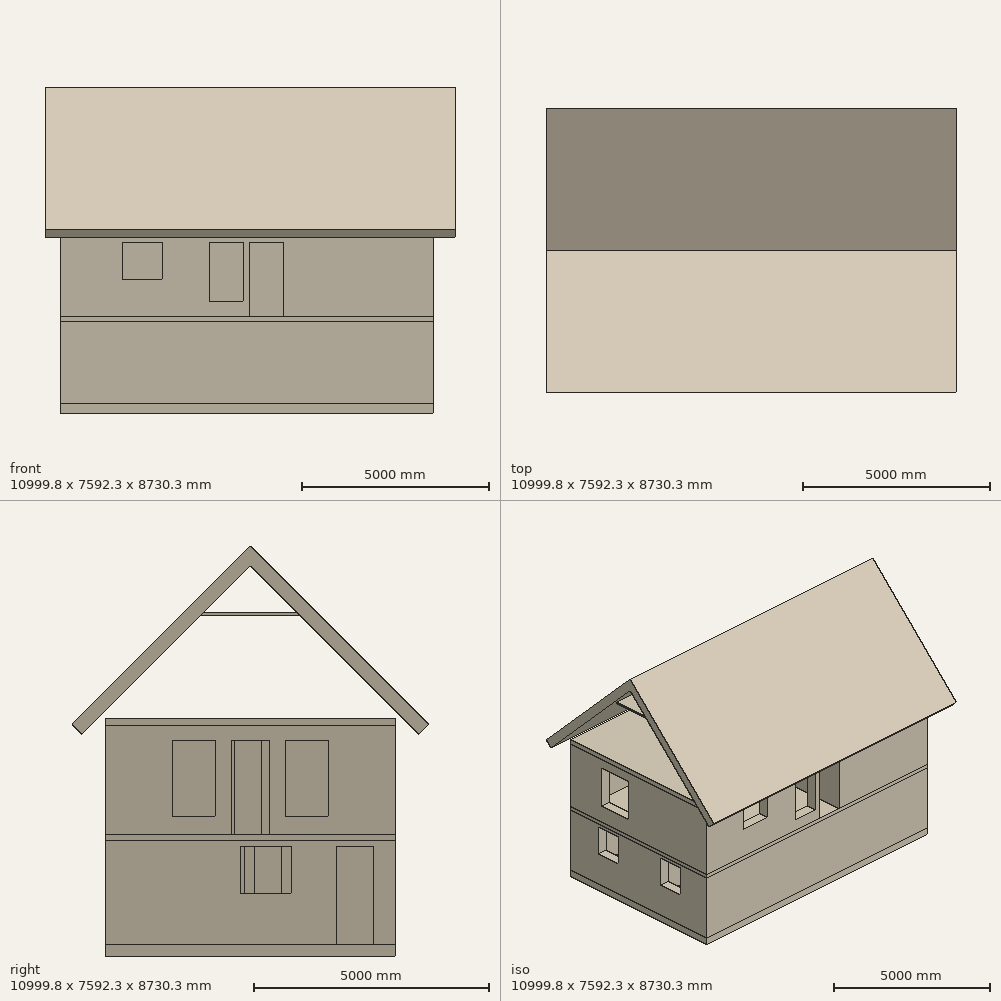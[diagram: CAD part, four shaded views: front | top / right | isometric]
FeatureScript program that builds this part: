
annotation { "Feature Type Name" : "Feature", "Feature Type Description" : "" }
export const myFeature = defineFeature(function(context is Context, id is Id, definition is map)
    precondition{}
    {
        {
            var Q0;
            Q0=qCreatedBy(makeId("Top.planeOp"),FACE);
            var sketch = newSketch(context, id + "F0", { "sketchPlane" : qUnion([Q0])});
            skLineSegment(sketch, "E0", {"start": v(0, 0) * mm, "end": v(-9312, 0) * mm});
            skLineSegment(sketch, "E1", {"start": v(0, 0) * mm, "end": v(0, -5472) * mm});
            skLineSegment(sketch, "E2", {"start": v(0, -5472) * mm, "end": v(-9312, -5472) * mm});
            skLineSegment(sketch, "E3", {"start": v(-9312, -5472) * mm, "end": v(-9312, 0) * mm});
            skLineSegment(sketch, "E4.0", {"start": v(348, 348) * mm, "end": v(-9660, 348) * mm});
            skLineSegment(sketch, "E4.1", {"start": v(348, 348) * mm, "end": v(348, -5820) * mm});
            skLineSegment(sketch, "E4.2", {"start": v(348, -5820) * mm, "end": v(-9660, -5820) * mm});
            skLineSegment(sketch, "E4.3", {"start": v(-9660, -5820) * mm, "end": v(-9660, 348) * mm});
            skSolve(sketch);
        }
        {
            var Q0;
            Q0=makeQuery(id+"F0.imprint","IMPRINT",FACE,{"disambiguationData":[TD([[makeQuery(id+"F0.imprint","IMPRINT",EDGE,{"derivedFrom":sQuery(id+"F0.wireOp",EDGE,"E0")}),-1.0]])]});
            extrude(context, id + "F1", {"entities" : qUnion([Q0]), "depth" : 2320 * mm});
        }
        {
            var Q0;
            Q0=qCreatedBy(makeId("Top.planeOp"),FACE);
            var sketch = newSketch(context, id + "F2", { "sketchPlane" : qUnion([Q0])});
            skLineSegment(sketch, "E5.bottom", {"start": v(-3552, 0) * mm, "end": v(-3660, 0) * mm});
            skLineSegment(sketch, "E5.top", {"start": v(-3552, -5472) * mm, "end": v(-3660, -5472) * mm});
            skLineSegment(sketch, "E5.left", {"start": v(-3552, 0) * mm, "end": v(-3552, -5472) * mm});
            skLineSegment(sketch, "E5.right", {"start": v(-3660, 0) * mm, "end": v(-3660, -5472) * mm});
            skLineSegment(sketch, "E6.bottom", {"start": v(-5652, 0) * mm, "end": v(-5760, 0) * mm});
            skLineSegment(sketch, "E6.top", {"start": v(-5652, -5472) * mm, "end": v(-5760, -5472) * mm});
            skLineSegment(sketch, "E6.left", {"start": v(-5652, 0) * mm, "end": v(-5652, -5472) * mm});
            skLineSegment(sketch, "E6.right", {"start": v(-5760, 0) * mm, "end": v(-5760, -5472) * mm});
            skSolve(sketch);
        }
        {
            var Q0;
            Q0 = qSketchRegion(id + "F2", true);
            var Q1;
            Q1=makeQuery(id+"F1.opExtrude","CAP_FACE",FACE,{"disambiguationData":[OSD([sQuery(id+"F0.wireOp",EDGE,"E0"),sQuery(id+"F0.wireOp",EDGE,"E1"),sQuery(id+"F0.wireOp",EDGE,"E2"),sQuery(id+"F0.wireOp",EDGE,"E3"),sQuery(id+"F0.wireOp",EDGE,"E4.0"),sQuery(id+"F0.wireOp",EDGE,"E4.1"),sQuery(id+"F0.wireOp",EDGE,"E4.2"),sQuery(id+"F0.wireOp",EDGE,"E4.3")])],"isStart":false});
            extrude(context, id + "F3", {"entities" : qUnion([Q0]), "operationType" : NewBodyOperationType.ADD, "endBound" : BoundingType.UP_TO_SURFACE, "endBoundEntityFace" : qUnion([Q1]), "depth" : 25 * mm});
        }
        {
            var Q0;
            Q0=qCreatedBy(makeId("Top.planeOp"),FACE);
            var sketch = newSketch(context, id + "F4", { "sketchPlane" : qUnion([Q0])});
            skLineSegment(sketch, "E7.bottom", {"start": v(-9312, -3072) * mm, "end": v(-5760, -3072) * mm});
            skLineSegment(sketch, "E7.top", {"start": v(-9312, -3180) * mm, "end": v(-5760, -3180) * mm});
            skLineSegment(sketch, "E7.left", {"start": v(-9312, -3072) * mm, "end": v(-9312, -3180) * mm});
            skLineSegment(sketch, "E7.right", {"start": v(-5760, -3072) * mm, "end": v(-5760, -3180) * mm});
            skSolve(sketch);
        }
        {
            var Q0;
            Q0 = qSketchRegion(id + "F4", true);
            var Q1;
            Q1=makeQuery(id+"F3.boolean.opBoolean","MERGE",FACE,{"derivedFrom":[makeQuery(id+"F1.opExtrude","CAP_FACE",FACE,{"disambiguationData":[OSD([sQuery(id+"F0.wireOp",EDGE,"E0"),sQuery(id+"F0.wireOp",EDGE,"E1"),sQuery(id+"F0.wireOp",EDGE,"E2"),sQuery(id+"F0.wireOp",EDGE,"E3"),sQuery(id+"F0.wireOp",EDGE,"E4.0"),sQuery(id+"F0.wireOp",EDGE,"E4.1"),sQuery(id+"F0.wireOp",EDGE,"E4.2"),sQuery(id+"F0.wireOp",EDGE,"E4.3")])],"isStart":false}),makeQuery(id+"F3.opExtrude","CAP_FACE",FACE,{"disambiguationData":[OSD([sQuery(id+"F2.wireOp",EDGE,"E5.bottom"),sQuery(id+"F2.wireOp",EDGE,"E5.top"),sQuery(id+"F2.wireOp",EDGE,"E5.left"),sQuery(id+"F2.wireOp",EDGE,"E5.right")])],"isStart":false}),makeQuery(id+"F3.opExtrude","CAP_FACE",FACE,{"disambiguationData":[OSD([sQuery(id+"F2.wireOp",EDGE,"E6.bottom"),sQuery(id+"F2.wireOp",EDGE,"E6.top"),sQuery(id+"F2.wireOp",EDGE,"E6.left"),sQuery(id+"F2.wireOp",EDGE,"E6.right")])],"isStart":false})]});
            extrude(context, id + "F5", {"entities" : qUnion([Q0]), "operationType" : NewBodyOperationType.ADD, "endBound" : BoundingType.UP_TO_SURFACE, "endBoundEntityFace" : qUnion([Q1]), "depth" : 25 * mm});
        }
        {
            var Q0;
            Q0=makeQuery(id+"F1.opExtrude","SWEPT_FACE",FACE,{"disambiguationData":[OSD([sQuery(id+"F0.wireOp",EDGE,"E4.2")])]});
            var sketch = newSketch(context, id + "F6", { "sketchPlane" : qUnion([Q0])});
            skLineSegment(sketch, "E8.bottom", {"start": v(-4572, 0) * mm, "end": v(-3660, 0) * mm});
            skLineSegment(sketch, "E8.top", {"start": v(-4572, 2000) * mm, "end": v(-3660, 2000) * mm});
            skLineSegment(sketch, "E8.left", {"start": v(-4572, 0) * mm, "end": v(-4572, 2000) * mm});
            skLineSegment(sketch, "E8.right", {"start": v(-3660, 0) * mm, "end": v(-3660, 2000) * mm});
            skLineSegment(sketch, "E9.bottom", {"start": v(-4740, 2000) * mm, "end": v(-5652, 2000) * mm});
            skLineSegment(sketch, "E9.top", {"start": v(-4740, 400) * mm, "end": v(-5652, 400) * mm});
            skLineSegment(sketch, "E9.left", {"start": v(-4740, 2000) * mm, "end": v(-4740, 400) * mm});
            skLineSegment(sketch, "E9.right", {"start": v(-5652, 2000) * mm, "end": v(-5652, 400) * mm});
            skLineSegment(sketch, "E10.bottom", {"start": v(-6912, 2000) * mm, "end": v(-7992, 2000) * mm});
            skLineSegment(sketch, "E10.top", {"start": v(-6912, 1000) * mm, "end": v(-7992, 1000) * mm});
            skLineSegment(sketch, "E10.left", {"start": v(-6912, 2000) * mm, "end": v(-6912, 1000) * mm});
            skLineSegment(sketch, "E10.right", {"start": v(-7992, 2000) * mm, "end": v(-7992, 1000) * mm});
            skSolve(sketch);
        }
        {
            var Q0;
            Q0 = qSketchRegion(id + "F6", true);
            extrude(context, id + "F7", {"entities" : qUnion([Q0]), "operationType" : NewBodyOperationType.REMOVE, "endBound" : BoundingType.UP_TO_NEXT, "oppositeDirection" : true, "depth" : 25 * mm});
        }
        {
            var Q0;
            Q0=makeQuery(id+"F1.opExtrude","SWEPT_FACE",FACE,{"disambiguationData":[OSD([sQuery(id+"F0.wireOp",EDGE,"E1")])]});
            var sketch = newSketch(context, id + "F8", { "sketchPlane" : qUnion([Q0])});
            skLineSegment(sketch, "E11.bottom", {"start": v(2340, 0) * mm, "end": v(3132, 0) * mm});
            skLineSegment(sketch, "E11.top", {"start": v(2340, 2000) * mm, "end": v(3132, 2000) * mm});
            skLineSegment(sketch, "E11.left", {"start": v(2340, 0) * mm, "end": v(2340, 2000) * mm});
            skLineSegment(sketch, "E11.right", {"start": v(3132, 0) * mm, "end": v(3132, 2000) * mm});
            skLineSegment(sketch, "E12.bottom", {"start": v(4392, 2000) * mm, "end": v(3480, 2000) * mm});
            skLineSegment(sketch, "E12.top", {"start": v(4392, 400) * mm, "end": v(3480, 400) * mm});
            skLineSegment(sketch, "E12.left", {"start": v(4392, 2000) * mm, "end": v(4392, 400) * mm});
            skLineSegment(sketch, "E12.right", {"start": v(3480, 2000) * mm, "end": v(3480, 400) * mm});
            skLineSegment(sketch, "E13.bottom", {"start": v(1992, 2000) * mm, "end": v(1080, 2000) * mm});
            skLineSegment(sketch, "E13.top", {"start": v(1992, 400) * mm, "end": v(1080, 400) * mm});
            skLineSegment(sketch, "E13.left", {"start": v(1992, 2000) * mm, "end": v(1992, 400) * mm});
            skLineSegment(sketch, "E13.right", {"start": v(1080, 2000) * mm, "end": v(1080, 400) * mm});
            skSolve(sketch);
        }
        {
            var Q0;
            Q0 = qSketchRegion(id + "F8", true);
            extrude(context, id + "F9", {"entities" : qUnion([Q0]), "operationType" : NewBodyOperationType.REMOVE, "endBound" : BoundingType.UP_TO_NEXT, "oppositeDirection" : true, "depth" : 25 * mm});
        }
        {
            var Q0;
            {var subQ0=sQuery(id+"F0.wireOp",EDGE,"E3");var subQ13=sQuery(id+"F0.wireOp",EDGE,"E0");Q0=makeQuery(id+"F5.boolean.opBoolean","SPLIT",FACE,{"disambiguationData":[TD([makeQuery(id+"F1.opExtrude","SWEPT_FACE",FACE,{"disambiguationData":[OSD([subQ13])]})])],"derivedFrom":makeQuery(id+"F1.opExtrude","SWEPT_FACE",FACE,{"disambiguationData":[OSD([subQ0])]})});}
            var sketch = newSketch(context, id + "F10", { "sketchPlane" : qUnion([Q0])});
            skLineSegment(sketch, "E14.bottom", {"start": v(-2272, 2000) * mm, "end": v(-1060, 2000) * mm});
            skLineSegment(sketch, "E14.top", {"start": v(-2272, 600) * mm, "end": v(-1060, 600) * mm});
            skLineSegment(sketch, "E14.left", {"start": v(-2272, 2000) * mm, "end": v(-2272, 600) * mm});
            skLineSegment(sketch, "E14.right", {"start": v(-1060, 2000) * mm, "end": v(-1060, 600) * mm});
            skSolve(sketch);
        }
        {
            var Q0;
            Q0 = qSketchRegion(id + "F10", true);
            extrude(context, id + "F11", {"entities" : qUnion([Q0]), "operationType" : NewBodyOperationType.REMOVE, "endBound" : BoundingType.UP_TO_NEXT, "oppositeDirection" : true, "depth" : 25 * mm});
        }
        {
            var Q0;
            Q0=makeQuery(id+"F7.boolean.opBoolean","MERGE",FACE,{"derivedFrom":[makeQuery(id+"F3.opExtrude","SWEPT_FACE",FACE,{"disambiguationData":[OSD([sQuery(id+"F2.wireOp",EDGE,"E5.right")])]}),makeQuery(id+"F7.opExtrude","SWEPT_FACE",FACE,{"disambiguationData":[OSD([sQuery(id+"F6.wireOp",EDGE,"E8.right")])]})]});
            var sketch = newSketch(context, id + "F12", { "sketchPlane" : qUnion([Q0])});
            skLineSegment(sketch, "E15.bottom", {"start": v(2500, 0) * mm, "end": v(3292, 0) * mm});
            skLineSegment(sketch, "E15.top", {"start": v(2500, 2100) * mm, "end": v(3292, 2100) * mm});
            skLineSegment(sketch, "E15.left", {"start": v(2500, 0) * mm, "end": v(2500, 2100) * mm});
            skLineSegment(sketch, "E15.right", {"start": v(3292, 0) * mm, "end": v(3292, 2100) * mm});
            skSolve(sketch);
        }
        {
            var Q0;
            Q0 = qSketchRegion(id + "F12", true);
            extrude(context, id + "F13", {"entities" : qUnion([Q0]), "operationType" : NewBodyOperationType.REMOVE, "endBound" : BoundingType.UP_TO_NEXT, "oppositeDirection" : true, "depth" : 25 * mm});
        }
        {
            var Q0;
            Q0=makeQuery(id+"F7.boolean.opBoolean","MERGE",FACE,{"derivedFrom":[makeQuery(id+"F3.opExtrude","SWEPT_FACE",FACE,{"disambiguationData":[OSD([sQuery(id+"F2.wireOp",EDGE,"E6.left")])]}),makeQuery(id+"F7.opExtrude","SWEPT_FACE",FACE,{"disambiguationData":[OSD([sQuery(id+"F6.wireOp",EDGE,"E9.right")])]})]});
            var sketch = newSketch(context, id + "F14", { "sketchPlane" : qUnion([Q0])});
            skLineSegment(sketch, "E16.bottom", {"start": v(-4332, 0) * mm, "end": v(-3540, 0) * mm});
            skLineSegment(sketch, "E16.top", {"start": v(-4332, 2100) * mm, "end": v(-3540, 2100) * mm});
            skLineSegment(sketch, "E16.left", {"start": v(-4332, 0) * mm, "end": v(-4332, 2100) * mm});
            skLineSegment(sketch, "E16.right", {"start": v(-3540, 0) * mm, "end": v(-3540, 2100) * mm});
            skLineSegment(sketch, "E17.bottom", {"start": v(-2280, 0) * mm, "end": v(-3072, 0) * mm});
            skLineSegment(sketch, "E17.top", {"start": v(-2280, 2100) * mm, "end": v(-3072, 2100) * mm});
            skLineSegment(sketch, "E17.left", {"start": v(-2280, 0) * mm, "end": v(-2280, 2100) * mm});
            skLineSegment(sketch, "E17.right", {"start": v(-3072, 0) * mm, "end": v(-3072, 2100) * mm});
            skSolve(sketch);
        }
        {
            var Q0;
            Q0 = qSketchRegion(id + "F14", true);
            extrude(context, id + "F15", {"entities" : qUnion([Q0]), "operationType" : NewBodyOperationType.REMOVE, "endBound" : BoundingType.UP_TO_NEXT, "oppositeDirection" : true, "depth" : 25 * mm});
        }
        {
            var Q0;
            Q0=qCreatedBy(makeId("Top.planeOp"),FACE);
            var sketch = newSketch(context, id + "F16", { "sketchPlane" : qUnion([Q0])});
            skLineSegment(sketch, "E18.bottom", {"start": v(348, 348) * mm, "end": v(-9660, 348) * mm});
            skLineSegment(sketch, "E18.top", {"start": v(348, -5820) * mm, "end": v(-9660, -5820) * mm});
            skLineSegment(sketch, "E18.left", {"start": v(348, 348) * mm, "end": v(348, -5820) * mm});
            skLineSegment(sketch, "E18.right", {"start": v(-9660, 348) * mm, "end": v(-9660, -5820) * mm});
            skLineSegment(sketch, "E19.bottom", {"start": v(-5652, 0) * mm, "end": v(-3660, 0) * mm});
            skLineSegment(sketch, "E19.top", {"start": v(-5652, -2100) * mm, "end": v(-3660, -2100) * mm});
            skLineSegment(sketch, "E19.left", {"start": v(-5652, 0) * mm, "end": v(-5652, -2100) * mm});
            skLineSegment(sketch, "E19.right", {"start": v(-3660, 0) * mm, "end": v(-3660, -2100) * mm});
            skSolve(sketch);
        }
        {
            var Q0;
            Q0 = qSketchRegion(id + "F16", true);
            extrude(context, id + "F17", {"entities" : qUnion([Q0]), "oppositeDirection" : true, "depth" : 130 * mm});
        }
        {
            var Q0;
            Q0=qCreatedBy(makeId("Top.planeOp"),FACE);
            cPlane(context, id + "F18", {"entities" : qUnion([Q0]), "cplaneType" : CPlaneType.OFFSET, "offset" : 2340 * mm, "oppositeDirection" : true, "width" : 150 * mm, "height" : 150 * mm});
        }
        {
            var Q0;
            Q0=qCreatedBy(id+"F18.planeOp",FACE);
            var sketch = newSketch(context, id + "F19", { "sketchPlane" : qUnion([Q0])});
            skLineSegment(sketch, "E20.0.0", {"start": v(348, -5820) * mm, "end": v(348, 348) * mm});
            skLineSegment(sketch, "E20.0.1", {"start": v(348, 348) * mm, "end": v(-9660, 348) * mm});
            skLineSegment(sketch, "E20.0.2", {"start": v(-9660, 348) * mm, "end": v(-9660, -5820) * mm});
            skLineSegment(sketch, "E20.0.3", {"start": v(-9660, -5820) * mm, "end": v(348, -5820) * mm});
            skLineSegment(sketch, "E21.bottom", {"start": v(-9312, 0) * mm, "end": v(-5760, 0) * mm});
            skLineSegment(sketch, "E21.top", {"start": v(-9312, -5472) * mm, "end": v(-5760, -5472) * mm});
            skLineSegment(sketch, "E21.left", {"start": v(-9312, 0) * mm, "end": v(-9312, -2712) * mm});
            skLineSegment(sketch, "E21.right", {"start": v(0, 0) * mm, "end": v(0, -5472) * mm});
            skLineSegment(sketch, "E22.0", {"start": v(-3552, 0) * mm, "end": v(-3552, -5472) * mm});
            skLineSegment(sketch, "E22.1", {"start": v(-3660, 0) * mm, "end": v(-3660, -4572) * mm});
            skLineSegment(sketch, "E22.2", {"start": v(-5652, 0) * mm, "end": v(-5652, -3792) * mm});
            skLineSegment(sketch, "E23", {"start": v(-5760, -5472) * mm, "end": v(-5760, -2820) * mm});
            skLineSegment(sketch, "E24.trimOffspring", {"start": v(-5652, -5472) * mm, "end": v(-3660, -5472) * mm});
            skLineSegment(sketch, "E25.trimOffspring", {"start": v(-3552, -5472) * mm, "end": v(0, -5472) * mm});
            skLineSegment(sketch, "E26.trimOffspring", {"start": v(-3552, 0) * mm, "end": v(0, 0) * mm});
            skLineSegment(sketch, "E27.trimOffspring", {"start": v(-5652, 0) * mm, "end": v(-3660, 0) * mm});
            skLineSegment(sketch, "E28", {"start": v(-9312, -2712) * mm, "end": v(-5760, -2712) * mm});
            skLineSegment(sketch, "E29", {"start": v(-9312, -2820) * mm, "end": v(-5760, -2820) * mm});
            skLineSegment(sketch, "E30.trimOffspring", {"start": v(-9312, -2820) * mm, "end": v(-9312, -5472) * mm});
            skLineSegment(sketch, "E31.trimOffspring", {"start": v(-5760, -2712) * mm, "end": v(-5760, 0) * mm});
            skLineSegment(sketch, "E32", {"start": v(-3660, -4572) * mm, "end": v(-4332, -4572) * mm});
            skLineSegment(sketch, "E33", {"start": v(-4332, -4572) * mm, "end": v(-4332, -3792) * mm});
            skLineSegment(sketch, "E34", {"start": v(-4332, -3792) * mm, "end": v(-5652, -3792) * mm});
            skLineSegment(sketch, "E35", {"start": v(-5652, -3900) * mm, "end": v(-4440, -3900) * mm});
            skLineSegment(sketch, "E36", {"start": v(-4440, -3900) * mm, "end": v(-4440, -4680) * mm});
            skLineSegment(sketch, "E37", {"start": v(-4440, -4680) * mm, "end": v(-3660, -4680) * mm});
            skLineSegment(sketch, "E38.trimOffspring", {"start": v(-5652, -3900) * mm, "end": v(-5652, -5472) * mm});
            skLineSegment(sketch, "E39.trimOffspring", {"start": v(-3660, -4680) * mm, "end": v(-3660, -5472) * mm});
            skSolve(sketch);
        }
        {
            var Q0;
            Q0 = qSketchRegion(id + "F19", true);
            var Q1;
            Q1=makeQuery(id+"F17.opExtrude","CAP_FACE",FACE,{"disambiguationData":[OSD([sQuery(id+"F16.wireOp",EDGE,"E18.bottom"),sQuery(id+"F16.wireOp",EDGE,"E18.top"),sQuery(id+"F16.wireOp",EDGE,"E18.left"),sQuery(id+"F16.wireOp",EDGE,"E18.right"),sQuery(id+"F16.wireOp",EDGE,"E19.bottom"),sQuery(id+"F16.wireOp",EDGE,"E19.top"),sQuery(id+"F16.wireOp",EDGE,"E19.left"),sQuery(id+"F16.wireOp",EDGE,"E19.right")])],"isStart":false});
            extrude(context, id + "F20", {"entities" : qUnion([Q0]), "endBound" : BoundingType.UP_TO_SURFACE, "endBoundEntityFace" : qUnion([Q1]), "depth" : 25 * mm});
        }
        {
            var Q0;
            Q0=makeQuery(id+"F20.opExtrude","CAP_FACE",FACE,{"disambiguationData":[OSD([sQuery(id+"F19.wireOp",EDGE,"E20.0.0"),sQuery(id+"F19.wireOp",EDGE,"E20.0.1"),sQuery(id+"F19.wireOp",EDGE,"E20.0.2"),sQuery(id+"F19.wireOp",EDGE,"E20.0.3"),sQuery(id+"F19.wireOp",EDGE,"E21.bottom"),sQuery(id+"F19.wireOp",EDGE,"E21.top"),sQuery(id+"F19.wireOp",EDGE,"E21.left"),sQuery(id+"F19.wireOp",EDGE,"E21.right"),sQuery(id+"F19.wireOp",EDGE,"E22.0"),sQuery(id+"F19.wireOp",EDGE,"E22.1"),sQuery(id+"F19.wireOp",EDGE,"E22.2"),sQuery(id+"F19.wireOp",EDGE,"E23"),sQuery(id+"F19.wireOp",EDGE,"E24.trimOffspring"),sQuery(id+"F19.wireOp",EDGE,"E25.trimOffspring"),sQuery(id+"F19.wireOp",EDGE,"E26.trimOffspring"),sQuery(id+"F19.wireOp",EDGE,"E27.trimOffspring")])],"isStart":true});
            var sketch = newSketch(context, id + "F21", { "sketchPlane" : qUnion([Q0])});
            skLineSegment(sketch, "E40.bottom", {"start": v(-9660, 5820) * mm, "end": v(348, 5820) * mm});
            skLineSegment(sketch, "E40.top", {"start": v(-9660, -348) * mm, "end": v(348, -348) * mm});
            skLineSegment(sketch, "E40.left", {"start": v(-9660, 5820) * mm, "end": v(-9660, -348) * mm});
            skLineSegment(sketch, "E40.right", {"start": v(348, 5820) * mm, "end": v(348, -348) * mm});
            skSolve(sketch);
        }
        {
            var Q0;
            Q0 = qSketchRegion(id + "F21", true);
            extrude(context, id + "F22", {"entities" : qUnion([Q0]), "depth" : 250 * mm});
        }
        {
            var Q0;
            Q0=makeQuery(id+"F5.boolean.opBoolean","MERGE",FACE,{"derivedFrom":[makeQuery(id+"F3.boolean.opBoolean","MERGE",FACE,{"derivedFrom":[makeQuery(id+"F1.opExtrude","CAP_FACE",FACE,{"disambiguationData":[OSD([sQuery(id+"F0.wireOp",EDGE,"E0"),sQuery(id+"F0.wireOp",EDGE,"E1"),sQuery(id+"F0.wireOp",EDGE,"E2"),sQuery(id+"F0.wireOp",EDGE,"E3"),sQuery(id+"F0.wireOp",EDGE,"E4.0"),sQuery(id+"F0.wireOp",EDGE,"E4.1"),sQuery(id+"F0.wireOp",EDGE,"E4.2"),sQuery(id+"F0.wireOp",EDGE,"E4.3")])],"isStart":false}),makeQuery(id+"F3.opExtrude","CAP_FACE",FACE,{"disambiguationData":[OSD([sQuery(id+"F2.wireOp",EDGE,"E5.bottom"),sQuery(id+"F2.wireOp",EDGE,"E5.top"),sQuery(id+"F2.wireOp",EDGE,"E5.left"),sQuery(id+"F2.wireOp",EDGE,"E5.right")])],"isStart":false}),makeQuery(id+"F3.opExtrude","CAP_FACE",FACE,{"disambiguationData":[OSD([sQuery(id+"F2.wireOp",EDGE,"E6.bottom"),sQuery(id+"F2.wireOp",EDGE,"E6.top"),sQuery(id+"F2.wireOp",EDGE,"E6.left"),sQuery(id+"F2.wireOp",EDGE,"E6.right")])],"isStart":false})]}),makeQuery(id+"F5.opExtrude","CAP_FACE",FACE,{"disambiguationData":[OSD([sQuery(id+"F4.wireOp",EDGE,"E7.bottom"),sQuery(id+"F4.wireOp",EDGE,"E7.top"),sQuery(id+"F4.wireOp",EDGE,"E7.left"),sQuery(id+"F4.wireOp",EDGE,"E7.right")])],"isStart":false})]});
            cPlane(context, id + "F23", {"entities" : qUnion([Q0]), "cplaneType" : CPlaneType.OFFSET, "offset" : 160 * mm, "width" : 150 * mm, "height" : 150 * mm});
        }
        {
            var Q0;
            Q0=makeQuery(id+"F1.opExtrude","SWEPT_FACE",FACE,{"disambiguationData":[OSD([sQuery(id+"F0.wireOp",EDGE,"E4.1")])]});
            var sketch = newSketch(context, id + "F24", { "sketchPlane" : qUnion([Q0])});
            skLineSegment(sketch, "E41", {"start": v(-2736, 2320) * mm, "end": v(-2736, 6140.26) * mm, "construction": true});
            skLineSegment(sketch, "E42", {"start": v(-2736, 6140.26) * mm, "end": v(-6532.13, 2344.13) * mm});
            skLineSegment(sketch, "E43", {"start": v(-6532.13, 2344.13) * mm, "end": v(-6320, 2132) * mm});
            skLineSegment(sketch, "E44", {"start": v(-6320, 2132) * mm, "end": v(-2736, 5716) * mm});
            skLineSegment(sketch, "E45.MirrorCS", {"start": v(848, 2132) * mm, "end": v(-2736, 5716) * mm});
            skLineSegment(sketch, "E46.MirrorCS", {"start": v(-2736, 6140.26) * mm, "end": v(1060.13, 2344.13) * mm});
            skLineSegment(sketch, "E47.MirrorCS", {"start": v(1060.13, 2344.13) * mm, "end": v(848, 2132) * mm});
            skLineSegment(sketch, "E48", {"start": v(-5820, 2480) * mm, "end": v(-5820, 2632) * mm, "construction": true});
            skSolve(sketch);
        }
        {
            var Q0;
            Q0 = qSketchRegion(id + "F24", true);
            extrude(context, id + "F25", {"entities" : qUnion([Q0]), "oppositeDirection" : true, "depth" : 10401.67 * mm, "hasSecondDirection" : true, "secondDirectionOppositeDirection" : false, "secondDirectionDepth" : 598.14 * mm});
        }
        {
            var Q0;
            Q0=qCreatedBy(id+"F23.planeOp",FACE);
            var sketch = newSketch(context, id + "F26", { "sketchPlane" : qUnion([Q0])});
            skLineSegment(sketch, "E49.0.0", {"start": v(348, -5820) * mm, "end": v(348, 348) * mm});
            skLineSegment(sketch, "E49.0.1", {"start": v(348, 348) * mm, "end": v(-9660, 348) * mm});
            skLineSegment(sketch, "E49.0.2", {"start": v(-9660, 348) * mm, "end": v(-9660, -5820) * mm});
            skLineSegment(sketch, "E49.0.3", {"start": v(-9660, -5820) * mm, "end": v(348, -5820) * mm});
            skLineSegment(sketch, "E50.bottom", {"start": v(-9312, -5472) * mm, "end": v(-5760, -5472) * mm});
            skLineSegment(sketch, "E50.top", {"start": v(-9312, 0) * mm, "end": v(-5760, 0) * mm});
            skLineSegment(sketch, "E50.left", {"start": v(-9312, -5472) * mm, "end": v(-9312, 0) * mm});
            skLineSegment(sketch, "E50.right", {"start": v(0, -5472) * mm, "end": v(0, 0) * mm});
            skLineSegment(sketch, "E51", {"start": v(-5760, 0) * mm, "end": v(-5760, -5472) * mm});
            skLineSegment(sketch, "E52", {"start": v(-5652, 0) * mm, "end": v(-5652, -5472) * mm});
            skLineSegment(sketch, "E53.trimOffspring", {"start": v(-5652, 0) * mm, "end": v(0, 0) * mm});
            skLineSegment(sketch, "E54.trimOffspring", {"start": v(-5652, -5472) * mm, "end": v(0, -5472) * mm});
            skSolve(sketch);
        }
        {
            var Q0;
            Q0 = qSketchRegion(id + "F26", true);
            var Q1;
            Q1=makeQuery(id+"F25.opExtrude","SWEPT_BODY",BODY,{"disambiguationData":[OSD([sQuery(id+"F24.wireOp",EDGE,"E42"),sQuery(id+"F24.wireOp",EDGE,"E43"),sQuery(id+"F24.wireOp",EDGE,"E44"),sQuery(id+"F24.wireOp",EDGE,"E45.MirrorCS"),sQuery(id+"F24.wireOp",EDGE,"E46.MirrorCS"),sQuery(id+"F24.wireOp",EDGE,"E47.MirrorCS")])]});
            extrude(context, id + "F27", {"entities" : qUnion([Q0]), "endBound" : BoundingType.UP_TO_BODY, "endBoundEntityBody" : qUnion([Q1]), "depth" : 3000 * mm});
        }
        {
            var Q0;
            Q0=makeQuery(id+"F5.boolean.opBoolean","MERGE",FACE,{"derivedFrom":[makeQuery(id+"F3.boolean.opBoolean","MERGE",FACE,{"derivedFrom":[makeQuery(id+"F1.opExtrude","CAP_FACE",FACE,{"disambiguationData":[OSD([sQuery(id+"F0.wireOp",EDGE,"E0"),sQuery(id+"F0.wireOp",EDGE,"E1"),sQuery(id+"F0.wireOp",EDGE,"E2"),sQuery(id+"F0.wireOp",EDGE,"E3"),sQuery(id+"F0.wireOp",EDGE,"E4.0"),sQuery(id+"F0.wireOp",EDGE,"E4.1"),sQuery(id+"F0.wireOp",EDGE,"E4.2"),sQuery(id+"F0.wireOp",EDGE,"E4.3")])],"isStart":false}),makeQuery(id+"F3.opExtrude","CAP_FACE",FACE,{"disambiguationData":[OSD([sQuery(id+"F2.wireOp",EDGE,"E5.bottom"),sQuery(id+"F2.wireOp",EDGE,"E5.top"),sQuery(id+"F2.wireOp",EDGE,"E5.left"),sQuery(id+"F2.wireOp",EDGE,"E5.right")])],"isStart":false}),makeQuery(id+"F3.opExtrude","CAP_FACE",FACE,{"disambiguationData":[OSD([sQuery(id+"F2.wireOp",EDGE,"E6.bottom"),sQuery(id+"F2.wireOp",EDGE,"E6.top"),sQuery(id+"F2.wireOp",EDGE,"E6.left"),sQuery(id+"F2.wireOp",EDGE,"E6.right")])],"isStart":false})]}),makeQuery(id+"F5.opExtrude","CAP_FACE",FACE,{"disambiguationData":[OSD([sQuery(id+"F4.wireOp",EDGE,"E7.bottom"),sQuery(id+"F4.wireOp",EDGE,"E7.top"),sQuery(id+"F4.wireOp",EDGE,"E7.left"),sQuery(id+"F4.wireOp",EDGE,"E7.right")])],"isStart":false})]});
            var sketch = newSketch(context, id + "F28", { "sketchPlane" : qUnion([Q0])});
            skLineSegment(sketch, "E55.1.0", {"start": v(348, -5820) * mm, "end": v(348, 348) * mm});
            skLineSegment(sketch, "E55.1.1", {"start": v(348, 348) * mm, "end": v(-9660, 348) * mm});
            skLineSegment(sketch, "E55.1.2", {"start": v(-9660, 348) * mm, "end": v(-9660, -5820) * mm});
            skLineSegment(sketch, "E55.1.3", {"start": v(-9660, -5820) * mm, "end": v(348, -5820) * mm});
            skLineSegment(sketch, "E56.bottom", {"start": v(-5652, 0) * mm, "end": v(-3660, 0) * mm});
            skLineSegment(sketch, "E56.top", {"start": v(-5652, -2160) * mm, "end": v(-3660, -2160) * mm});
            skLineSegment(sketch, "E56.left", {"start": v(-5652, 0) * mm, "end": v(-5652, -2160) * mm});
            skLineSegment(sketch, "E56.right", {"start": v(-3660, 0) * mm, "end": v(-3660, -2160) * mm});
            skSolve(sketch);
        }
        {
            var Q0;
            Q0 = qSketchRegion(id + "F28", true);
            var Q1;
            Q1=qCreatedBy(id+"F23.planeOp",FACE);
            extrude(context, id + "F29", {"entities" : qUnion([Q0]), "endBound" : BoundingType.UP_TO_SURFACE, "endBoundEntityFace" : qUnion([Q1]), "depth" : 160 * mm});
        }
        {
            var Q0;
            Q0=makeQuery(id+"F27.opExtrude","SWEPT_FACE",FACE,{"disambiguationData":[OSD([sQuery(id+"F26.wireOp",EDGE,"E49.0.0")])]});
            var sketch = newSketch(context, id + "F30", { "sketchPlane" : qUnion([Q0])});
            skLineSegment(sketch, "E57.bottom", {"start": v(-3772, 4680) * mm, "end": v(-1700, 4680) * mm});
            skLineSegment(sketch, "E57.top", {"start": v(-3722, 4730) * mm, "end": v(-1750, 4730) * mm});
            skLineSegment(sketch, "E57.left", {"start": v(-3772, 4680) * mm, "end": v(-3722, 4730) * mm});
            skLineSegment(sketch, "E57.right", {"start": v(-1700, 4680) * mm, "end": v(-1750, 4730) * mm});
            skSolve(sketch);
        }
        {
            var Q0;
            Q0 = qSketchRegion(id + "F30", true);
            extrude(context, id + "F31", {"entities" : qUnion([Q0]), "operationType" : NewBodyOperationType.REMOVE, "endBound" : BoundingType.THROUGH_ALL, "oppositeDirection" : true, "depth" : 25 * mm});
        }
        {
            var Q0;
            Q0=makeQuery(id+"F20.opExtrude","SWEPT_FACE",FACE,{"disambiguationData":[OSD([sQuery(id+"F19.wireOp",EDGE,"E31.trimOffspring")])]});
            var sketch = newSketch(context, id + "F32", { "sketchPlane" : qUnion([Q0])});
            skLineSegment(sketch, "E58.bottom", {"start": v(1860, -2340) * mm, "end": v(2652, -2340) * mm});
            skLineSegment(sketch, "E58.top", {"start": v(1860, -240) * mm, "end": v(2652, -240) * mm});
            skLineSegment(sketch, "E58.left", {"start": v(1860, -2340) * mm, "end": v(1860, -240) * mm});
            skLineSegment(sketch, "E58.right", {"start": v(2652, -2340) * mm, "end": v(2652, -240) * mm});
            skLineSegment(sketch, "E59.bottom", {"start": v(3672, -2340) * mm, "end": v(2880, -2340) * mm});
            skLineSegment(sketch, "E59.top", {"start": v(3672, -240) * mm, "end": v(2880, -240) * mm});
            skLineSegment(sketch, "E59.left", {"start": v(3672, -2340) * mm, "end": v(3672, -240) * mm});
            skLineSegment(sketch, "E59.right", {"start": v(2880, -2340) * mm, "end": v(2880, -240) * mm});
            skSolve(sketch);
        }
        {
            var Q0;
            Q0 = qSketchRegion(id + "F32", true);
            extrude(context, id + "F33", {"entities" : qUnion([Q0]), "operationType" : NewBodyOperationType.REMOVE, "endBound" : BoundingType.UP_TO_NEXT, "oppositeDirection" : true, "depth" : 25 * mm});
        }
        {
            var Q0;
            Q0=makeQuery(id+"F20.opExtrude","SWEPT_FACE",FACE,{"disambiguationData":[OSD([sQuery(id+"F19.wireOp",EDGE,"E34")])]});
            var sketch = newSketch(context, id + "F34", { "sketchPlane" : qUnion([Q0])});
            skLineSegment(sketch, "E60.bottom", {"start": v(4580, -2340) * mm, "end": v(5252, -2340) * mm});
            skLineSegment(sketch, "E60.top", {"start": v(4580, -240) * mm, "end": v(5252, -240) * mm});
            skLineSegment(sketch, "E60.left", {"start": v(4580, -2340) * mm, "end": v(4580, -240) * mm});
            skLineSegment(sketch, "E60.right", {"start": v(5252, -2340) * mm, "end": v(5252, -240) * mm});
            skSolve(sketch);
        }
        {
            var Q0;
            Q0 = qSketchRegion(id + "F34", true);
            extrude(context, id + "F35", {"entities" : qUnion([Q0]), "operationType" : NewBodyOperationType.REMOVE, "endBound" : BoundingType.UP_TO_NEXT, "oppositeDirection" : true, "depth" : 25 * mm});
        }
        {
            var Q0;
            Q0=makeQuery(id+"F20.opExtrude","SWEPT_FACE",FACE,{"disambiguationData":[OSD([sQuery(id+"F19.wireOp",EDGE,"E22.1")])]});
            var sketch = newSketch(context, id + "F36", { "sketchPlane" : qUnion([Q0])});
            skLineSegment(sketch, "E61.bottom", {"start": v(2862, -2340) * mm, "end": v(2070, -2340) * mm});
            skLineSegment(sketch, "E61.top", {"start": v(2862, -240) * mm, "end": v(2070, -240) * mm});
            skLineSegment(sketch, "E61.left", {"start": v(2862, -2340) * mm, "end": v(2862, -240) * mm});
            skLineSegment(sketch, "E61.right", {"start": v(2070, -2340) * mm, "end": v(2070, -240) * mm});
            skSolve(sketch);
        }
        {
            var Q0;
            Q0 = qSketchRegion(id + "F36", true);
            extrude(context, id + "F37", {"entities" : qUnion([Q0]), "operationType" : NewBodyOperationType.REMOVE, "endBound" : BoundingType.UP_TO_NEXT, "oppositeDirection" : true, "depth" : 25 * mm});
        }
        {
            var Q0;
            Q0=makeQuery(id+"F20.opExtrude","SWEPT_FACE",FACE,{"disambiguationData":[OSD([sQuery(id+"F19.wireOp",EDGE,"E21.right")])]});
            var sketch = newSketch(context, id + "F38", { "sketchPlane" : qUnion([Q0])});
            skLineSegment(sketch, "E62.bottom", {"start": v(120, -2340) * mm, "end": v(912, -2340) * mm});
            skLineSegment(sketch, "E62.top", {"start": v(120, -240) * mm, "end": v(912, -240) * mm});
            skLineSegment(sketch, "E62.left", {"start": v(120, -2340) * mm, "end": v(120, -240) * mm});
            skLineSegment(sketch, "E62.right", {"start": v(912, -2340) * mm, "end": v(912, -240) * mm});
            skLineSegment(sketch, "E63.bottom", {"start": v(1860, -240) * mm, "end": v(2952, -240) * mm});
            skLineSegment(sketch, "E63.top", {"start": v(1860, -1240) * mm, "end": v(2952, -1240) * mm});
            skLineSegment(sketch, "E63.left", {"start": v(1860, -240) * mm, "end": v(1860, -1240) * mm});
            skLineSegment(sketch, "E63.right", {"start": v(2952, -240) * mm, "end": v(2952, -1240) * mm});
            skSolve(sketch);
        }
        {
            var Q0;
            Q0 = qSketchRegion(id + "F38", true);
            extrude(context, id + "F39", {"entities" : qUnion([Q0]), "operationType" : NewBodyOperationType.REMOVE, "endBound" : BoundingType.UP_TO_NEXT, "oppositeDirection" : true, "depth" : 25 * mm});
        }
        {
            var Q0;
            Q0=makeQuery(id+"F20.opExtrude","SWEPT_FACE",FACE,{"disambiguationData":[OSD([sQuery(id+"F19.wireOp",EDGE,"E30.trimOffspring")])]});
            var sketch = newSketch(context, id + "F40", { "sketchPlane" : qUnion([Q0])});
            skLineSegment(sketch, "E64.bottom", {"start": v(-4632, -240) * mm, "end": v(-3720, -240) * mm});
            skLineSegment(sketch, "E64.top", {"start": v(-4632, -1240) * mm, "end": v(-3720, -1240) * mm});
            skLineSegment(sketch, "E64.left", {"start": v(-4632, -240) * mm, "end": v(-4632, -1240) * mm});
            skLineSegment(sketch, "E64.right", {"start": v(-3720, -240) * mm, "end": v(-3720, -1240) * mm});
            skLineSegment(sketch, "E65.bottom", {"start": v(-1812, -240) * mm, "end": v(-900, -240) * mm});
            skLineSegment(sketch, "E65.top", {"start": v(-1812, -1240) * mm, "end": v(-900, -1240) * mm});
            skLineSegment(sketch, "E65.left", {"start": v(-1812, -240) * mm, "end": v(-1812, -1240) * mm});
            skLineSegment(sketch, "E65.right", {"start": v(-900, -240) * mm, "end": v(-900, -1240) * mm});
            skSolve(sketch);
        }
        {
            var Q0;
            Q0 = qSketchRegion(id + "F40", true);
            extrude(context, id + "F41", {"entities" : qUnion([Q0]), "operationType" : NewBodyOperationType.REMOVE, "endBound" : BoundingType.UP_TO_NEXT, "oppositeDirection" : true, "depth" : 25 * mm});
        }
        {
            var Q0;
            {var subQ0=sQuery(id+"F26.wireOp",EDGE,"E50.left");var subQ2=sQuery(id+"F26.wireOp",EDGE,"E50.bottom");Q0=makeQuery(id+"F31.boolean.opBoolean","SPLIT",FACE,{"disambiguationData":[TD([makeQuery(id+"F27.opExtrude","SWEPT_FACE",FACE,{"disambiguationData":[OSD([subQ2])]})])],"derivedFrom":makeQuery(id+"F27.opExtrude","SWEPT_FACE",FACE,{"disambiguationData":[OSD([subQ0])]})});}
            var sketch = newSketch(context, id + "F42", { "sketchPlane" : qUnion([Q0])});
            skLineSegment(sketch, "E66.bottom", {"start": v(-3286, 4480) * mm, "end": v(-2186, 4480) * mm});
            skLineSegment(sketch, "E66.top", {"start": v(-3286, 3380) * mm, "end": v(-2186, 3380) * mm});
            skLineSegment(sketch, "E66.left", {"start": v(-3286, 4480) * mm, "end": v(-3286, 3380) * mm});
            skLineSegment(sketch, "E66.right", {"start": v(-2186, 4480) * mm, "end": v(-2186, 3380) * mm});
            skLineSegment(sketch, "E67", {"start": v(-2736, 4680) * mm, "end": v(-2736, 4480) * mm, "construction": true});
            skSolve(sketch);
        }
        {
            var Q0;
            Q0 = qSketchRegion(id + "F42", true);
            extrude(context, id + "F43", {"entities" : qUnion([Q0]), "operationType" : NewBodyOperationType.REMOVE, "endBound" : BoundingType.UP_TO_NEXT, "oppositeDirection" : true, "depth" : 25 * mm});
        }
        {
            var Q0;
            {var subQ0=sQuery(id+"F26.wireOp",EDGE,"E52");var subQ1=sQuery(id+"F26.wireOp",EDGE,"E53.trimOffspring");Q0=makeQuery(id+"F31.boolean.opBoolean","SPLIT",FACE,{"disambiguationData":[TD([makeQuery(id+"F27.opExtrude","SWEPT_FACE",FACE,{"disambiguationData":[OSD([subQ1])]})])],"derivedFrom":makeQuery(id+"F27.opExtrude","SWEPT_FACE",FACE,{"disambiguationData":[OSD([subQ0])]})});}
            var sketch = newSketch(context, id + "F44", { "sketchPlane" : qUnion([Q0])});
            skLineSegment(sketch, "E68.bottom", {"start": v(-2860, 2480) * mm, "end": v(-3652, 2480) * mm});
            skLineSegment(sketch, "E68.top", {"start": v(-2860, 4580) * mm, "end": v(-3652, 4580) * mm});
            skLineSegment(sketch, "E68.left", {"start": v(-2860, 2480) * mm, "end": v(-2860, 4580) * mm});
            skLineSegment(sketch, "E68.right", {"start": v(-3652, 2480) * mm, "end": v(-3652, 4580) * mm});
            skSolve(sketch);
        }
        {
            var Q0;
            Q0 = qSketchRegion(id + "F44", true);
            extrude(context, id + "F45", {"entities" : qUnion([Q0]), "operationType" : NewBodyOperationType.REMOVE, "endBound" : BoundingType.UP_TO_NEXT, "oppositeDirection" : true, "depth" : 25 * mm});
        }
        {
            var Q0;
            {var subQ0=sQuery(id+"F26.wireOp",EDGE,"E50.right");var subQ1=sQuery(id+"F26.wireOp",EDGE,"E53.trimOffspring");Q0=makeQuery(id+"F31.boolean.opBoolean","SPLIT",FACE,{"disambiguationData":[TD([makeQuery(id+"F27.opExtrude","SWEPT_FACE",FACE,{"disambiguationData":[OSD([subQ1])]})])],"derivedFrom":makeQuery(id+"F27.opExtrude","SWEPT_FACE",FACE,{"disambiguationData":[OSD([subQ0])]})});}
            var sketch = newSketch(context, id + "F46", { "sketchPlane" : qUnion([Q0])});
            skLineSegment(sketch, "E69.bottom", {"start": v(1830, 2480) * mm, "end": v(3642, 2480) * mm});
            skLineSegment(sketch, "E69.top", {"start": v(1830, 4480) * mm, "end": v(3642, 4480) * mm});
            skLineSegment(sketch, "E69.left", {"start": v(1830, 2480) * mm, "end": v(1830, 4480) * mm});
            skLineSegment(sketch, "E69.right", {"start": v(3642, 2480) * mm, "end": v(3642, 4480) * mm});
            skLineSegment(sketch, "E70", {"start": v(2736, 4480) * mm, "end": v(2736, 4680) * mm, "construction": true});
            skSolve(sketch);
        }
        {
            var Q0;
            Q0 = qSketchRegion(id + "F46", true);
            extrude(context, id + "F47", {"entities" : qUnion([Q0]), "operationType" : NewBodyOperationType.REMOVE, "endBound" : BoundingType.UP_TO_NEXT, "oppositeDirection" : true, "depth" : 25 * mm});
        }
        {
            var Q0;
            Q0 = qSketchRegion(id + "F30", true);
            var Q1;
            {var subQ0=sQuery(id+"F26.wireOp",EDGE,"E49.0.2");var subQ2=sQuery(id+"F26.wireOp",EDGE,"E49.0.1");Q1=makeQuery(id+"F31.boolean.opBoolean","SPLIT",FACE,{"disambiguationData":[TD([makeQuery(id+"F27.opExtrude","SWEPT_FACE",FACE,{"disambiguationData":[OSD([subQ2])]})])],"derivedFrom":makeQuery(id+"F27.opExtrude","SWEPT_FACE",FACE,{"disambiguationData":[OSD([subQ0])]})});}
            extrude(context, id + "F48", {"entities" : qUnion([Q0]), "endBound" : BoundingType.UP_TO_SURFACE, "oppositeDirection" : true, "endBoundEntityFace" : qUnion([Q1]), "depth" : 25 * mm});
        }
        {
            var Q0;
            Q0=makeQuery(id+"F31.boolean.opBoolean","SPLIT",BODY,{"disambiguationData":[OD(3.0)],"derivedFrom":makeQuery(id+"F27.opExtrude","SWEPT_BODY",BODY,{"disambiguationData":[OSD([sQuery(id+"F26.wireOp",EDGE,"E49.0.0"),sQuery(id+"F26.wireOp",EDGE,"E49.0.1"),sQuery(id+"F26.wireOp",EDGE,"E49.0.2"),sQuery(id+"F26.wireOp",EDGE,"E49.0.3"),sQuery(id+"F26.wireOp",EDGE,"E50.bottom"),sQuery(id+"F26.wireOp",EDGE,"E50.top"),sQuery(id+"F26.wireOp",EDGE,"E50.left"),sQuery(id+"F26.wireOp",EDGE,"E50.right"),sQuery(id+"F26.wireOp",EDGE,"E51"),sQuery(id+"F26.wireOp",EDGE,"E52"),sQuery(id+"F26.wireOp",EDGE,"E53.trimOffspring"),sQuery(id+"F26.wireOp",EDGE,"E54.trimOffspring")])]})});
            deleteBodies(context, id + "F49", {"entities" : qUnion([Q0])});
        }
    });
